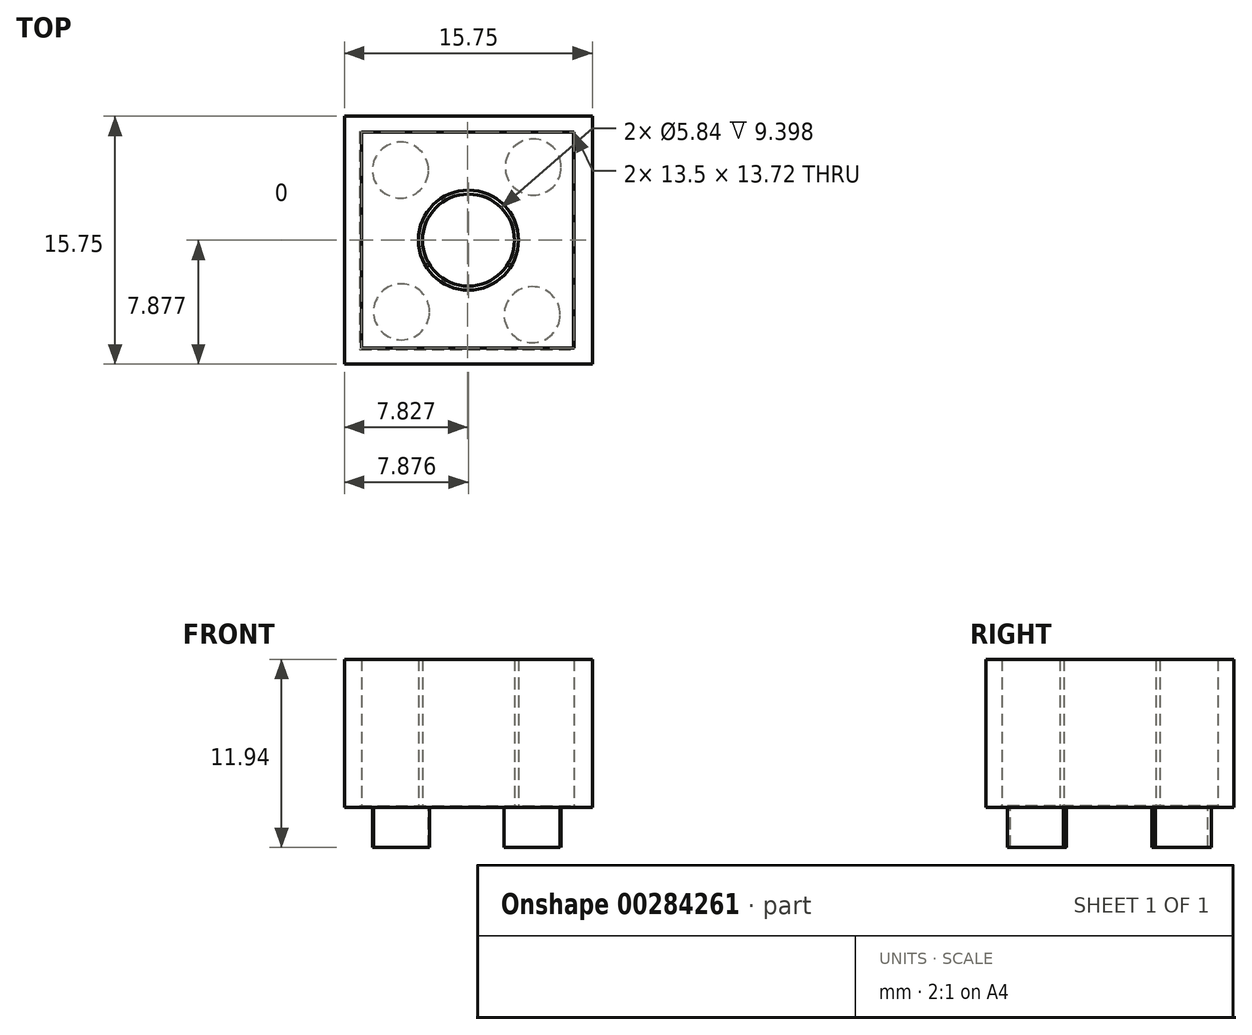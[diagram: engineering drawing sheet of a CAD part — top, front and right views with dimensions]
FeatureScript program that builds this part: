
annotation { "Feature Type Name" : "Feature", "Feature Type Description" : "" }
export const myFeature = defineFeature(function(context is Context, id is Id, definition is map)
    precondition{}
    {
        {
            var Q0;
            Q0=qCreatedBy(makeId("Top.planeOp"),FACE);
            var sketch = newSketch(context, id + "F0", { "sketchPlane" : qUnion([Q0])});
            skLineSegment(sketch, "E0.bottom", {"start": v(-15.75, -41.1) * mm, "end": v(0, -41.1) * mm});
            skLineSegment(sketch, "E0.top", {"start": v(-15.75, -25.36) * mm, "end": v(0, -25.36) * mm});
            skLineSegment(sketch, "E0.left", {"start": v(-15.75, -41.1) * mm, "end": v(-15.75, -25.36) * mm});
            skLineSegment(sketch, "E0.right", {"start": v(0, -41.1) * mm, "end": v(0, -25.36) * mm});
            skLineSegment(sketch, "E1.bottom", {"start": v(-14.67, -26.37) * mm, "end": v(-1.17, -26.37) * mm});
            skLineSegment(sketch, "E1.top", {"start": v(-14.67, -40.1) * mm, "end": v(-1.17, -40.1) * mm});
            skLineSegment(sketch, "E1.left", {"start": v(-14.67, -26.37) * mm, "end": v(-14.67, -40.1) * mm});
            skLineSegment(sketch, "E1.right", {"start": v(-1.17, -26.37) * mm, "end": v(-1.17, -40.1) * mm});
            skCircle(sketch, "E2", {"center": v(-7.87, -33.23) * mm, "radius": 3.18 * mm});
            skCircle(sketch, "E3", {"center": v(-7.87, -33.23) * mm, "radius": 2.92 * mm});
            skSolve(sketch);
        }
        {
            var Q0;
            Q0=makeQuery(id+"F0.imprint","IMPRINT",FACE,{"disambiguationData":[TD([[makeQuery(id+"F0.imprint","IMPRINT",EDGE,{"derivedFrom":sQuery(id+"F0.wireOp",EDGE,"E0.bottom")}),1.0]])]});
            extrude(context, id + "F1", {"entities" : qUnion([Q0]), "depth" : 9.4 * mm});
        }
        {
            var Q0;
            Q0=makeQuery(id+"F0.imprint","IMPRINT",FACE,{"disambiguationData":[TD([[makeQuery(id+"F0.imprint","IMPRINT",EDGE,{"derivedFrom":sQuery(id+"F0.wireOp",EDGE,"E2")}),1.0]])]});
            extrude(context, id + "F2", {"entities" : qUnion([Q0]), "depth" : 9.4 * mm});
        }
        {
            var Q0;
            Q0=qCreatedBy(makeId("Top.planeOp"),FACE);
            var sketch = newSketch(context, id + "F3", { "sketchPlane" : qUnion([Q0])});
            skLineSegment(sketch, "E4.bottom", {"start": v(-14.78, -26.35) * mm, "end": v(-1.2, -26.35) * mm});
            skLineSegment(sketch, "E4.top", {"start": v(-14.78, -40.18) * mm, "end": v(-1.2, -40.18) * mm});
            skLineSegment(sketch, "E4.left", {"start": v(-14.78, -26.35) * mm, "end": v(-14.78, -40.18) * mm});
            skLineSegment(sketch, "E4.right", {"start": v(-1.2, -26.35) * mm, "end": v(-1.2, -40.18) * mm});
            skSolve(sketch);
        }
        {
            var Q0;
            Q0 = qSketchRegion(id + "F3", true);
            extrude(context, id + "F4", {"entities" : qUnion([Q0]), "depth" : 0.1 * mm});
        }
        {
            var Q0;
            Q0=qCreatedBy(makeId("Top.planeOp"),FACE);
            var sketch = newSketch(context, id + "F5", { "sketchPlane" : qUnion([Q0])});
            skCircle(sketch, "E5", {"center": v(-3.83, -37.97) * mm, "radius": 1.78 * mm});
            skCircle(sketch, "E6", {"center": v(-3.76, -28.6) * mm, "radius": 1.78 * mm});
            skCircle(sketch, "E7", {"center": v(-12.2, -28.79) * mm, "radius": 1.78 * mm});
            skCircle(sketch, "E8", {"center": v(-12.12, -37.79) * mm, "radius": 1.78 * mm});
            skSolve(sketch);
        }
        {
            var Q0;
            Q0 = qSketchRegion(id + "F5", true);
            extrude(context, id + "F6", {"entities" : qUnion([Q0]), "operationType" : NewBodyOperationType.ADD, "oppositeDirection" : true, "depth" : 2.54 * mm});
        }
    });
